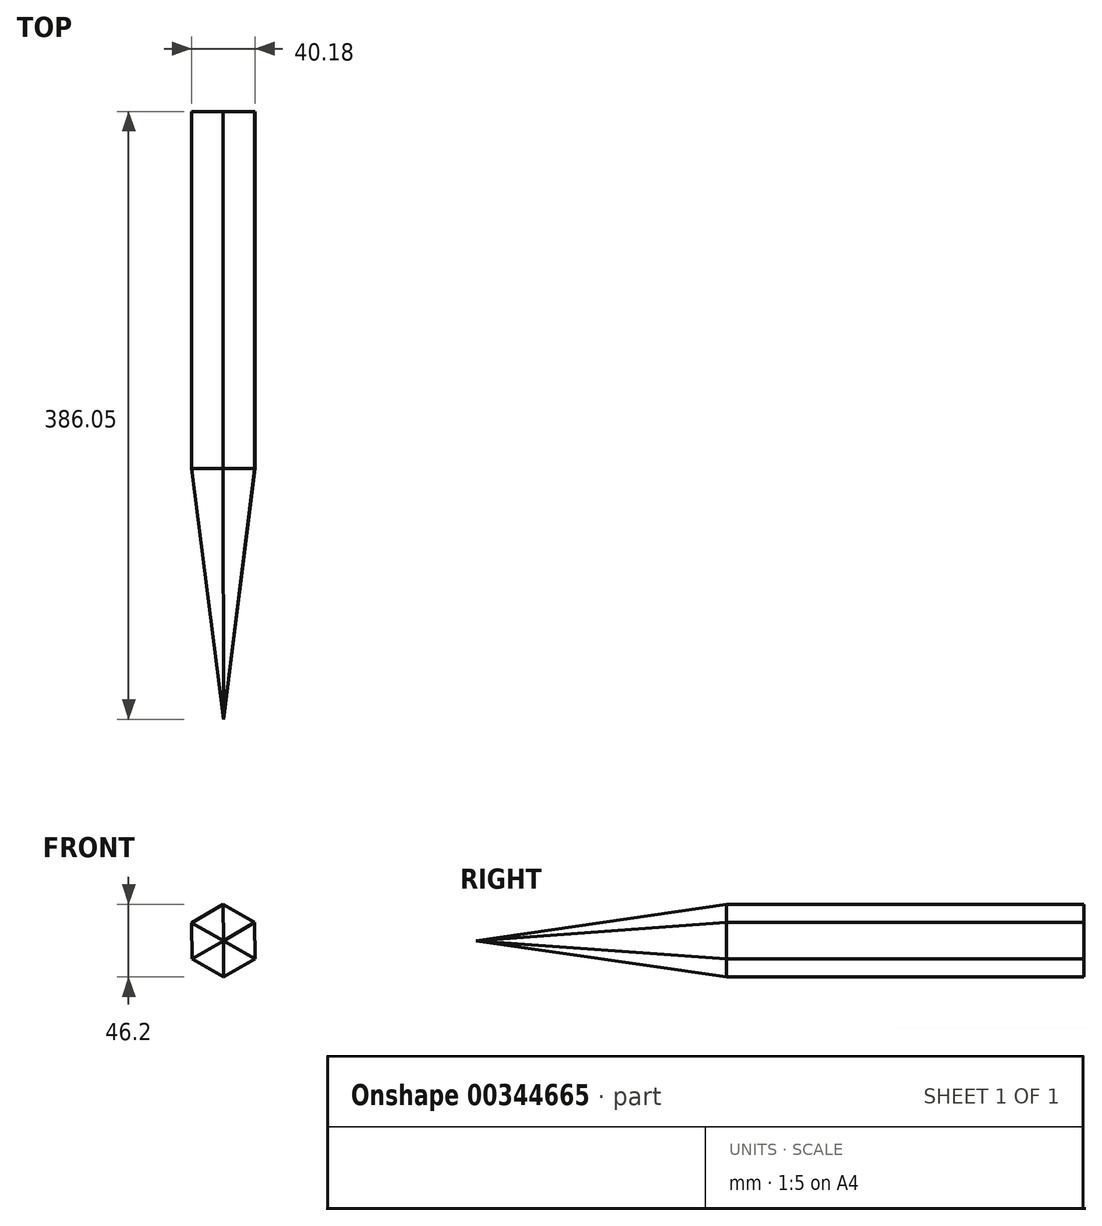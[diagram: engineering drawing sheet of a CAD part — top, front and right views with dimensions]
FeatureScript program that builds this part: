
annotation { "Feature Type Name" : "Feature", "Feature Type Description" : "" }
export const myFeature = defineFeature(function(context is Context, id is Id, definition is map)
    precondition{}
    {
        {
            var Q0;
            Q0=qCreatedBy(makeId("Front.planeOp"),FACE);
            var sketch = newSketch(context, id + "F0", { "sketchPlane" : qUnion([Q0])});
            skCircle(sketch, "E0.cCircle", {"center": v(0, 0) * mm, "radius": 20 * mm, "construction": true});
            skLineSegment(sketch, "E0.0", {"start": v(-0.16, 23.1) * mm, "end": v(19.93, 11.7) * mm});
            skLineSegment(sketch, "E0.1", {"start": v(19.93, 11.7) * mm, "end": v(20.1, -11.4) * mm});
            skLineSegment(sketch, "E0.2", {"start": v(20.1, -11.4) * mm, "end": v(0.16, -23.1) * mm});
            skLineSegment(sketch, "E0.3", {"start": v(0.16, -23.1) * mm, "end": v(-19.93, -11.7) * mm});
            skLineSegment(sketch, "E0.4", {"start": v(-19.93, -11.7) * mm, "end": v(-20.1, 11.4) * mm});
            skLineSegment(sketch, "E0.5", {"start": v(-20.1, 11.4) * mm, "end": v(-0.16, 23.1) * mm});
            skPoint(sketch, "E0.0.midPoint", {"position": v(9.88, 17.4) * mm});
            skSolve(sketch);
        }
        {
            var Q0;
            Q0=qCreatedBy(makeId("Top.planeOp"),FACE);
            var sketch = newSketch(context, id + "F1", { "sketchPlane" : qUnion([Q0])});
            skLineSegment(sketch, "E1", {"start": v(0, 106.65) * mm, "end": v(0, -120.24) * mm});
            skSolve(sketch);
        }
        {
            var Q0;
            Q0=makeQuery(id+"F0.imprint","IMPRINT",FACE,{"disambiguationData":[TD([[makeQuery(id+"F0.imprint","IMPRINT",EDGE,{"derivedFrom":sQuery(id+"F0.wireOp",EDGE,"E0.0")}),-1.0]])]});
            var Q1;
            Q1=sQuery(id+"F1.wireOp",EDGE,"E1");
            sweep(context, id + "F2", {"profiles" : qUnion([Q0]), "path" : qUnion([Q1])});
        }
        {
            var Q0;
            Q0=qCreatedBy(makeId("Front.planeOp"),FACE);
            cPlane(context, id + "F3", {"entities" : qUnion([Q0]), "cplaneType" : CPlaneType.OFFSET, "offset" : 279.4 * mm, "width" : 152.4 * mm, "height" : 152.4 * mm});
        }
        {
            var Q0;
            Q0=qCreatedBy(id+"F3.planeOp",FACE);
            var sketch = newSketch(context, id + "F4", { "sketchPlane" : qUnion([Q0])});
            skCircle(sketch, "E2", {"center": v(0, 0) * mm, "radius": 3.75 * mm});
            skSolve(sketch);
        }
        {
            var Q1;
            Q1=makeQuery(id+"F2.opSweep","CAP_FACE",FACE,{"disambiguationData":[OSD([sQuery(id+"F0.wireOp",EDGE,"E0.0"),sQuery(id+"F0.wireOp",EDGE,"E0.1"),sQuery(id+"F0.wireOp",EDGE,"E0.2"),sQuery(id+"F0.wireOp",EDGE,"E0.3"),sQuery(id+"F0.wireOp",EDGE,"E0.4"),sQuery(id+"F0.wireOp",EDGE,"E0.5"),sQuery(id+"F1.wireOp",VERTEX,"E1.end")])],"isStart":false});
            var Q2;
            Q2=sQuery(id+"F4.wireOp",VERTEX,"E2.center");
            loft(context, id + "F5", {"operationType" : NewBodyOperationType.ADD, "sheetProfilesArray" : [{ "sheetProfileEntities" : qUnion([Q1]) }, { "sheetProfileEntities" : qUnion([Q2]) }]});
        }
    });
